# Revit family: Hager-Vega_D-IP41-syst-NoHosted-BE-fr
name_source: partatom
category: Electrical Equipment
units: mm (PartAtom-declared; Revit-internal decimal feet)

## family parameters
Always vertical = Yes
Cut with Voids When Loaded = No
Panel Configuration = Two Columns, Circuits Across
Part Type = Panelboard
Room Calculation Point = No
Round Connector Dimension = Use Diameter
Shared = No
Work Plane-Based = Yes

## types (14) — shared parameters
Default Elevation = 1219 mm
EF000003 - mode de pose = EV000384 - saillie
EF000007 - couleur = EV000202 - blanc
EF000008 - largeur = 550 mm
EF000049 - profondeur = 193 mm  [stored 0.633202 ft]
EF000116 - numéro RAL = 9010
EF000339 - type de capot = EV004216 - porte
EF001062 - finition CEM = No
EF001088 - possibilité de montage en saillie = Yes
EF001131 - profondeur intérieure = 193 mm  [stored 0.633202 ft]
EF001134 - rail DIN = Yes
EF001596 - matériau du boîtier/corps = EV000154 - autre
EF002950 - largeur en nombre de modules = 24
EF005474 - indice de protection (IP) = EV006416 - IP41
EF006306 - avec serrure = No
EF015776 - borne de mise à la terre = Yes
EF015777 - borne à conducteur neutre = No
EF015941 - porte pour transmission du signal = No
HG000001 - nombre de colonnes = 1
HG000002 - avec porte = Yes
HG000003 - Gamme = Vega D
HG000005 - Epaisseur = 3 mm  [stored 0.00984252 ft]
HG000006 - Encastré = No
HG000009 - Porte à double battant = No
HG000010 - Portes asymétriques = No
HG000017 - Distance entre pôles = 18 mm  [stored 0.0590551 ft]
Manufacturer = Hager
Type Comments = Vega D
zero-valued in all types: EF000218 - profondeur d'encastrement, EF000332 - hauteur d'encastrement, EF000846 - largeur d'encastrement, HG000007 - Nombre de colonnes vides

## per-type parameters (varying)
| type | EF000040 - hauteur | EF000118 - avec cadre/support de montage | EF000266 - nombre de rangées | EF004462 - type de fermeture | EF006244 - couvercle/porte transparent(e) | EF009212 - finition du couvercle | HG000004 - Référence fabricant | HG000008 - Nombre de rangées vides | HG000011 - Rangées du bas vides | Model |
| Saillie IP41 L550 H1050 P193 24 Modules - FD62BN | 1050 mm | No | 6 | EV000154 - autre | No | EV000116 - fermé | FD62BN | 0 | No | FD62BN |
| Saillie IP41 L550 H1050 P193 24 Modules - FD62CN | 1050 mm | No | 6 | EV000154 - autre | Yes | EV009916 - avec échancrure | FD62CN | 0 | No | FD62CN |
| Saillie IP41 L550 H1200 P193 24 Modules - FD72BN | 1200 mm | No | 7 | EV000154 - autre | No | EV000116 - fermé | FD72BN | 0 | No | FD72BN |
| Saillie IP41 L550 H1200 P193 24 Modules - FD72CN | 1200 mm | No | 7 | EV000154 - autre | Yes | EV009916 - avec échancrure | FD72CN | 0 | No | FD72CN |
| Saillie IP41 L550 H450 P193 24 Modules - FD22BN | 450 mm  [stored 1.47638 ft] | No | 2 |  | No | EV000116 - fermé | FD22BN | 0 | No | FD22BN |
| Saillie IP41 L550 H450 P193 24 Modules - FD22CN | 450 mm  [stored 1.47638 ft] | No | 2 |  | Yes | EV009916 - avec échancrure | FD22CN | 0 | No | FD22CN |
| Saillie IP41 L550 H600 P193 24 Modules - FD32BN | 600 mm | No | 3 | EV000154 - autre | No | EV000116 - fermé | FD32BN | 0 | No | FD32BN |
| Saillie IP41 L550 H600 P193 24 Modules - FD32CN | 600 mm | No | 3 | EV000154 - autre | Yes | EV000116 - fermé | FD32CN | 0 | No | FD32CN |
| Saillie IP41 L550 H750 P193 24 Modules - FD42BMN | 750 mm  [stored 2.46063 ft] | Yes | 1 | EV000154 - autre | No | EV000116 - fermé | FD42BMN | 3 | Yes | FD42BMN |
| Saillie IP41 L550 H750 P193 24 Modules - FD42BN | 750 mm  [stored 2.46063 ft] | No | 4 | EV000154 - autre | No | EV000116 - fermé | FD42BN | 0 | No | FD42BN |
| Saillie IP41 L550 H750 P193 24 Modules - FD42CN | 750 mm  [stored 2.46063 ft] | No | 4 | EV000154 - autre | Yes | EV009916 - avec échancrure | FD42CN | 0 | No | FD42CN |
| Saillie IP41 L550 H900 P193 24 Modules - FD52BMN | 900 mm  [stored 2.95276 ft] | Yes | 2 | EV000154 - autre | No | EV000116 - fermé | FD52BMN | 3 | Yes | FD52BMN |
| Saillie IP41 L550 H900 P193 24 Modules - FD52BN | 900 mm  [stored 2.95276 ft] | No | 5 | EV000154 - autre | No | EV000116 - fermé | FD52BN | 0 | No | FD52BN |
| Saillie IP41 L550 H900 P193 24 Modules - FD52CN | 900 mm  [stored 2.95276 ft] | No | 5 | EV000154 - autre | Yes | EV009916 - avec échancrure | FD52CN | 0 | No | FD52CN |

note: [stored X ft] marks values corroborated as IEEE doubles in the binary element streams (Revit-internal decimal feet)

## geometry (parser evidence)
native form markers: Sweep x13
no freeform markers — native parametric forms only
